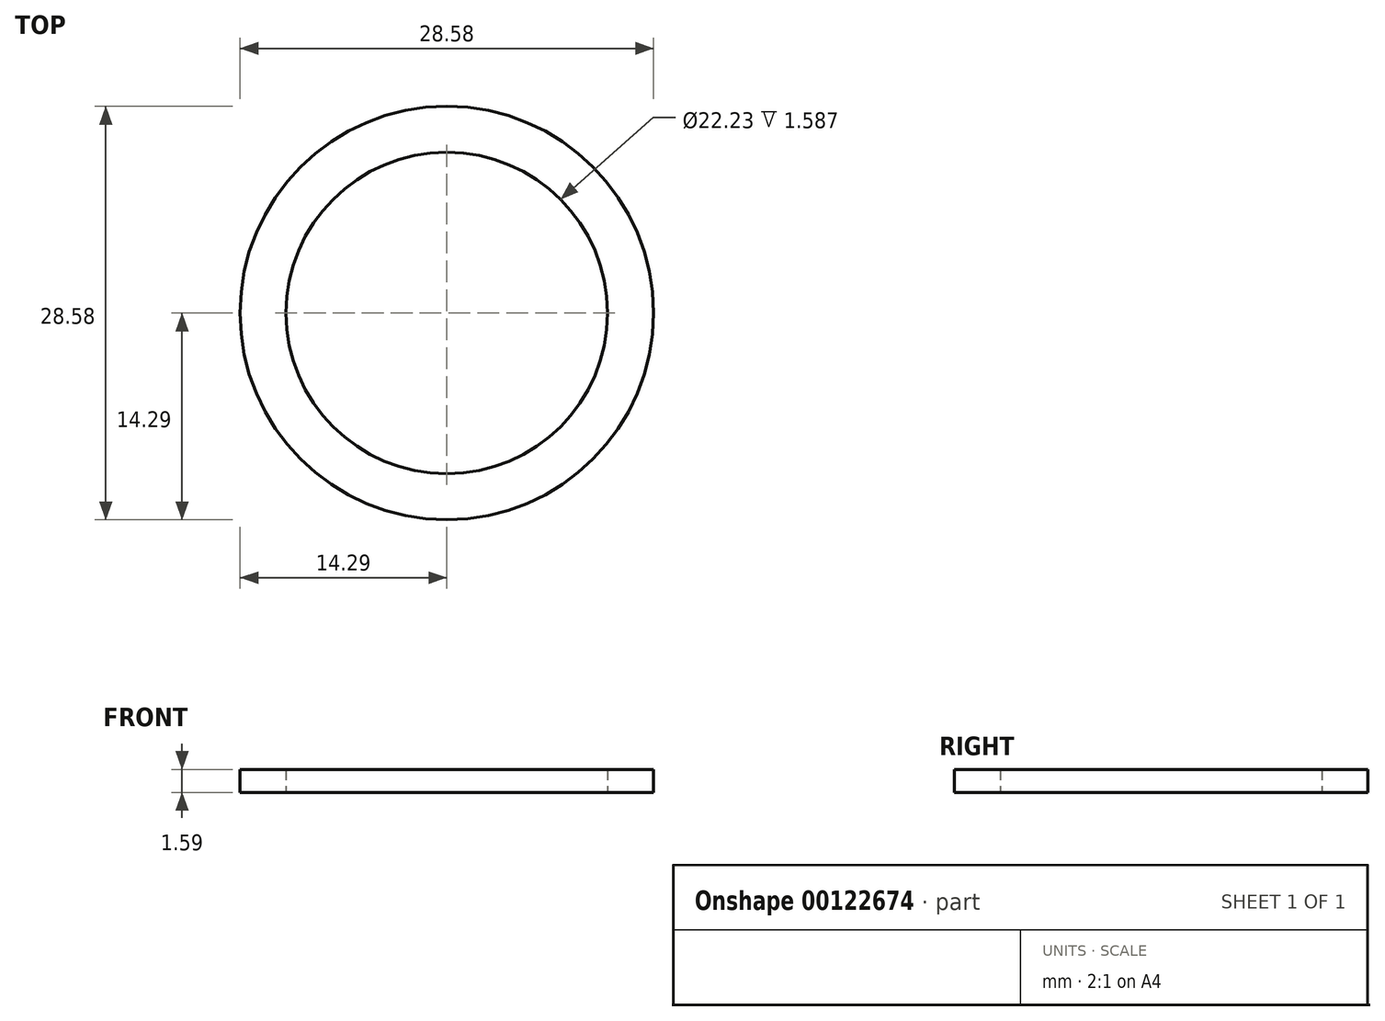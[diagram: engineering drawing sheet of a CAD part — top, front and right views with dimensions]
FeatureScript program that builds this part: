
annotation { "Feature Type Name" : "Feature", "Feature Type Description" : "" }
export const myFeature = defineFeature(function(context is Context, id is Id, definition is map)
    precondition{}
    {
        {
            var Q0;
            Q0=qCreatedBy(makeId("Top.planeOp"),FACE);
            var sketch = newSketch(context, id + "F0", { "sketchPlane" : qUnion([Q0])});
            skCircle(sketch, "E0", {"center": v(0, 0) * mm, "radius": 11.11 * mm});
            skCircle(sketch, "E1", {"center": v(0, 0) * mm, "radius": 14.29 * mm});
            skSolve(sketch);
        }
        {
            var Q0;
            Q0=makeQuery(id+"F0.imprint","IMPRINT",FACE,{"disambiguationData":[TD([[makeQuery(id+"F0.imprint","IMPRINT",EDGE,{"derivedFrom":sQuery(id+"F0.wireOp",EDGE,"E0")}),-1.0]])]});
            extrude(context, id + "F1", {"entities" : qUnion([Q0]), "depth" : 1.59 * mm});
        }
    });
